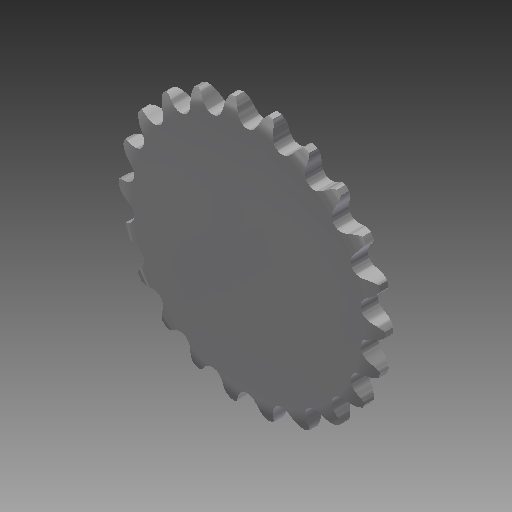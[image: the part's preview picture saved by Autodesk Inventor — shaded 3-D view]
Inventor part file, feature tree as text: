
AUTODESK INVENTOR PART (.ipt)
format: ipt  version: 2017 (Build 210142000, 142)  size: 613,376 bytes
history: native  units: mm
features: other x6, extrude x2, pattern_linear x1, pattern_circular x1
ambient origin geometry x8: Origin, YZ Plane, XZ Plane, XY Plane, X Axis, Y Axis, Z Axis, Center Point
bodies: Solid1 (feature_tree)
feature tree (10):
  other  "Theoretical Tooth Profile"
  other  "Tooth Profile"
  other  "Section Profile"
  other  "Shroud"
  other  "Strand"
  pattern_linear  "Strand Pattern"  Spacing1=44.619381mm  [1 undecoded]
  extrude  "Theoretical Tooth"  Depth=2.855993mm
  extrude  "Tooth"  Depth=1.697355mm
  pattern_circular  "Tooth Pattern"  [2 undecoded]
  other  "Timing Plane"
note: 3 required parameter values undecoded (feature->parameter linkage not recoverable at this tier; creation-order binding heuristic only, values carry confidence <= 0.55)
